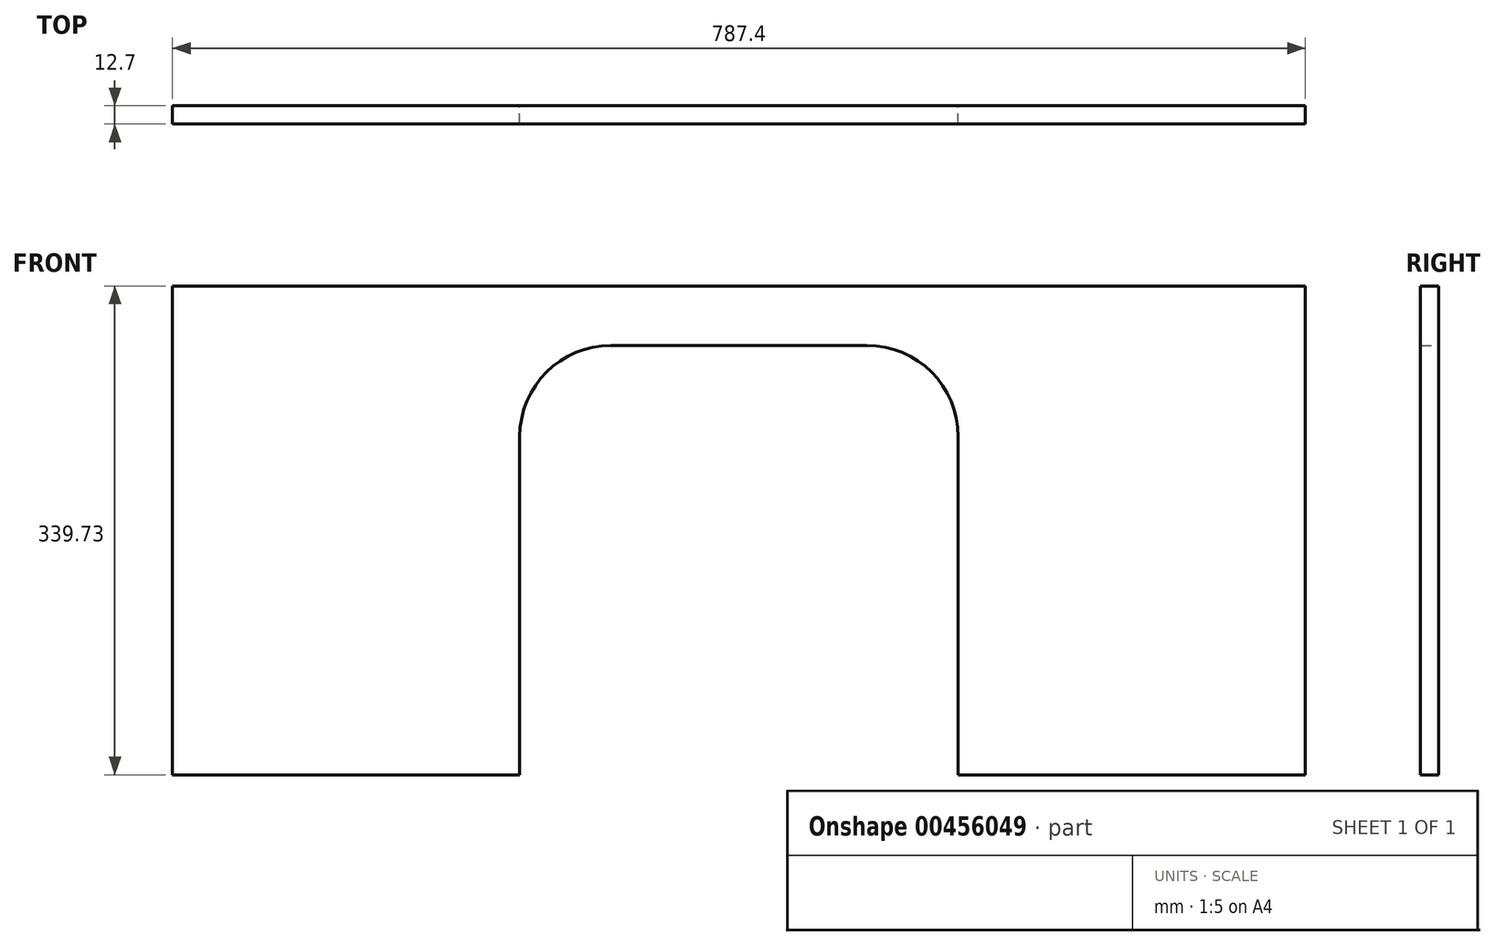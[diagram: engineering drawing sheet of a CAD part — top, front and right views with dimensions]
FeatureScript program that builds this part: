
annotation { "Feature Type Name" : "Feature", "Feature Type Description" : "" }
export const myFeature = defineFeature(function(context is Context, id is Id, definition is map)
    precondition{}
    {
        {
            var Q0;
            Q0=qCreatedBy(makeId("Front.planeOp"),FACE);
            var sketch = newSketch(context, id + "F0", { "sketchPlane" : qUnion([Q0])});
            skLineSegment(sketch, "E0.bottom", {"start": v(0, 0) * mm, "end": v(-787.4, 0) * mm});
            skLineSegment(sketch, "E0.top", {"start": v(0, 339.73) * mm, "end": v(-787.4, 339.72) * mm});
            skLineSegment(sketch, "E0.left", {"start": v(0, 0) * mm, "end": v(0, 339.73) * mm});
            skLineSegment(sketch, "E0.right", {"start": v(-787.4, 0) * mm, "end": v(-787.4, 339.72) * mm});
            skLineSegment(sketch, "E1", {"start": v(-774.7, 339.72) * mm, "end": v(-774.7, 0) * mm});
            skLineSegment(sketch, "E2", {"start": v(-393.7, 339.73) * mm, "end": v(-393.7, 0) * mm, "construction": true});
            skLineSegment(sketch, "E3.MirrorCS", {"start": v(-12.7, 339.72) * mm, "end": v(-12.7, 0) * mm});
            skLineSegment(sketch, "E4.bottom", {"start": v(-393.7, 0) * mm, "end": v(-546.1, 0) * mm});
            skLineSegment(sketch, "E4.top", {"start": v(-393.7, 298.45) * mm, "end": v(-482.6, 298.45) * mm});
            skLineSegment(sketch, "E4.left", {"start": v(-393.7, 0) * mm, "end": v(-393.7, 298.45) * mm});
            skLineSegment(sketch, "E4.right", {"start": v(-546.1, 0) * mm, "end": v(-546.1, 234.95) * mm});
            skLineSegment(sketch, "E5.MirrorCS", {"start": v(-393.7, 0) * mm, "end": v(-241.3, 0) * mm});
            skPoint(sketch, "E6.visualSharp", {"position": v(-546.1, 298.45) * mm});
            skArc(sketch, "E6.filletArc", {"start": v(-482.6, 298.45) * mm, "mid": v(-527.5, 279.85) * mm, "end": v(-546.1, 234.95) * mm});
            skLineSegment(sketch, "E7.MirrorCS", {"start": v(-393.7, 298.45) * mm, "end": v(-304.8, 298.45) * mm});
            skArc(sketch, "E8.MirrorCS", {"start": v(-304.8, 298.45) * mm, "mid": v(-259.9, 279.85) * mm, "end": v(-241.3, 234.95) * mm});
            skLineSegment(sketch, "E9.MirrorCS", {"start": v(-241.3, 0) * mm, "end": v(-241.3, 234.95) * mm});
            skSolve(sketch);
        }
        {
            var Q0;
            {var subQ4=sQuery(id+"F0.wireOp",EDGE,"E1");Q0=makeQuery(id+"F0.imprint","IMPRINT",FACE,{"disambiguationData":[TD([[makeQuery(id+"F0.imprint","IMPRINT",EDGE,{"derivedFrom":subQ4}),1.0]])]});}
            var Q1;
            {var subQ0=sQuery(id+"F0.wireOp",EDGE,"E0.left");Q1=makeQuery(id+"F0.imprint","IMPRINT",FACE,{"disambiguationData":[TD([[makeQuery(id+"F0.imprint","IMPRINT",EDGE,{"derivedFrom":subQ0}),1.0]])]});}
            var Q2;
            {var subQ0=sQuery(id+"F0.wireOp",EDGE,"E0.right");Q2=makeQuery(id+"F0.imprint","IMPRINT",FACE,{"disambiguationData":[TD([[makeQuery(id+"F0.imprint","IMPRINT",EDGE,{"derivedFrom":subQ0}),-1.0]])]});}
            extrude(context, id + "F1", {"entities" : qUnion([Q0, Q1, Q2]), "depth" : 12.7 * mm});
        }
    });
